# Revit family: Shower-Slidebar-KOHLER-K-12879T_1
name_source: partatom
category: Specialty Equipment
revit_build: Autodesk Revit 2017 (Build: 20160225_1515(x64)
units: mm (PartAtom-declared; Revit-internal decimal feet)

## family parameters
Cut with Voids When Loaded = No
Host = Face
OmniClass Number = 23.40.20.21.44
OmniClass Title = Shower Rods, Curtains
Part Type = Normal
Room Calculation Point = No
Round Connector Dimension = Use Diameter
Shared = No

## types (4) — shared parameters
ADA Compliant = No
Assembly Code = D2010700
Date Modified = 09/16/2020
Default Elevation = 42"
Height = 32 3/8"
Length = 2"
Manufacturer = KOHLER Co.
Master Format 2014 = 10 28 00
Master Format 2014 Name = Toilet, Bath, and Laundry Accessories
Material = Premium Metal Construction
Product Documentation Link = https://files.kohler.com.cn
Product Name = SLIDE BAR
Product Page URL = https://www.kohler.com.cn
URL = http://www.kohler.com.cn
WaterSense Certified = No
Width = 7 7/8"

## per-type parameters (varying)
| type | Description | Finish | Model | Type |
| CP-Polished Chrome | SLIDE BAR, 800MM | Kohler-Metal-CP-Polished_Chrome | K-12879T-CP | 1 |
| AF-Vibrant French Gold | SLIDING BAR, (80CM) | Kohler-Metal-AF-Vibrant_French_Gold | K-12879T-AF | 2 |
| BN-Vibrant Brushed Nickel | SLIDING BAR, 800MM | Kohler-Metal-BN-Vibrant_Brushed_Nickel | K-12879T-BN | 3 |
| SN-Vibrant Polished Nickel | SLIDING BAR, 800MM | Kohler-Metal-SN-Vibrant_Polished_Nickel | K-12879T-SN | 4 |

## geometry (parser evidence)
native form markers: Sweep x5
no freeform markers — native parametric forms only
